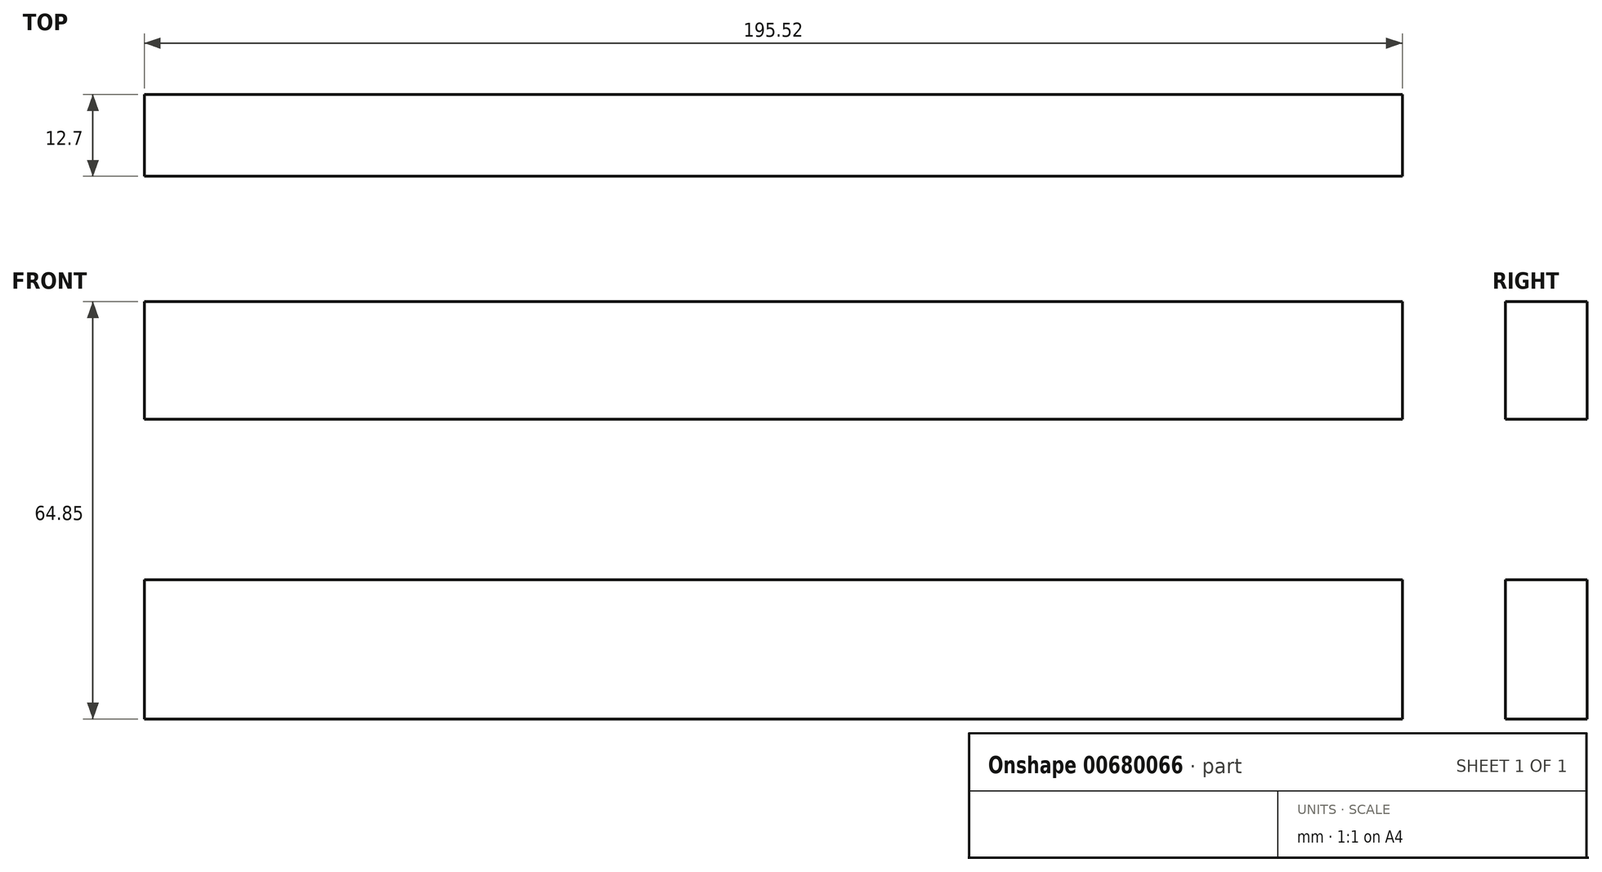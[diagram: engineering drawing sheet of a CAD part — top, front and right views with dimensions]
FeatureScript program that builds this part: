
annotation { "Feature Type Name" : "Feature", "Feature Type Description" : "" }
export const myFeature = defineFeature(function(context is Context, id is Id, definition is map)
    precondition{}
    {
        {
            var Q0;
            Q0=qCreatedBy(makeId("Front.planeOp"),FACE);
            var sketch = newSketch(context, id + "F0", { "sketchPlane" : qUnion([Q0])});
            skLineSegment(sketch, "E0.bottom", {"start": v(-97.76, 10.8) * mm, "end": v(97.76, 10.8) * mm});
            skLineSegment(sketch, "E0.top", {"start": v(-97.76, -10.8) * mm, "end": v(97.76, -10.8) * mm});
            skLineSegment(sketch, "E0.left", {"start": v(-97.76, 10.8) * mm, "end": v(-97.76, -10.8) * mm});
            skLineSegment(sketch, "E0.right", {"start": v(97.76, 10.8) * mm, "end": v(97.76, -10.8) * mm});
            skPoint(sketch, "E0.middle", {"position": v(0, 0) * mm});
            skLineSegment(sketch, "E1.bottom", {"start": v(-97.76, 54.04) * mm, "end": v(97.76, 54.04) * mm});
            skLineSegment(sketch, "E1.top", {"start": v(-97.76, 35.79) * mm, "end": v(97.76, 35.79) * mm});
            skLineSegment(sketch, "E1.left", {"start": v(-97.76, 54.04) * mm, "end": v(-97.76, 35.79) * mm});
            skLineSegment(sketch, "E1.right", {"start": v(97.76, 54.04) * mm, "end": v(97.76, 35.79) * mm});
            skPoint(sketch, "E1.middle", {"position": v(0, 44.92) * mm});
            skSolve(sketch);
        }
        {
            var Q0;
            Q0 = qSketchRegion(id + "F0", true);
            extrude(context, id + "F1", {"entities" : qUnion([Q0]), "depth" : 12.7 * mm, "offsetDistance" : 25.4 * mm});
        }
    });
